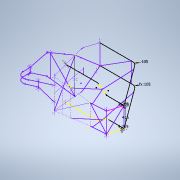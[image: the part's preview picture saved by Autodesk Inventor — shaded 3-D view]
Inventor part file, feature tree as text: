
AUTODESK INVENTOR PART (.ipt)
format: ipt  version: 2022 (Build 260153000, 153)  size: 223,744 bytes
history: native  units: mm
features: other x18, sketch x3, plane x2
ambient origin geometry x8: Origin, YZ Plane, XZ Plane, XY Plane, X Axis, Y Axis, Z Axis, Center Point
feature tree (23):
  other  "Assoalho"
  other  "Plano de trabalho2"
  other  "Plano de trabalho6"
  other  "Plano de trabalho7"
  other  "Plano de trabalho9"
  other  "angulo de ataque"
  other  "FAB SUSP"
  other  "plano do tanque"
  other  "plano fire"
  other  "Firewall"
  other  "Posição eixo final"
  other  "TRASEIRA"
  other  "OSIM"
  other  "Boneco De M"
  other  "ref0"
  other  "ref1"
  other  "Plano de trabalho15"
  plane  "Work Plane21"
  other  "SIM"
  sketch  "Sketch30"  dims[d5=175.0mm]
  plane  "Work Plane23"
  sketch  "Sketch31"  dims[d10=290.0mm d42=32.114058mm d117=318.406mm d118=318.406mm d133=160.0mm d141=13.788101mm d169=800.0mm d170=500.0mm d171=490.0mm d172=600.0mm d175=15.400159mm d178=330.0mm d179=10.754719mm d180=310.0mm d181=20.071286mm d182=23.88704mm d183=549.790416mm d188=570.0mm d189=10.0mm d190=25.0mm d225=120.0mm d236=15.7mm d302=280.0mm d303=60.0mm d305=770.0mm d307=120.0mm d309=110.0mm d310=110.0mm d311=105.0mm d312=105.0mm d313=0.0mm d317=105.0mm d318=15.0mm d320=100.0mm d321=90.0mm d322=90.0mm d323=200.0mm d324=200.0mm d326=416.0mm d327=105.0mm d328=105.0mm d329=4.269mm d330=4.269mm d332=20.0mm d333=20.0mm d334=20.0mm d335=20.0mm]
  sketch  "3D Sketch15"
